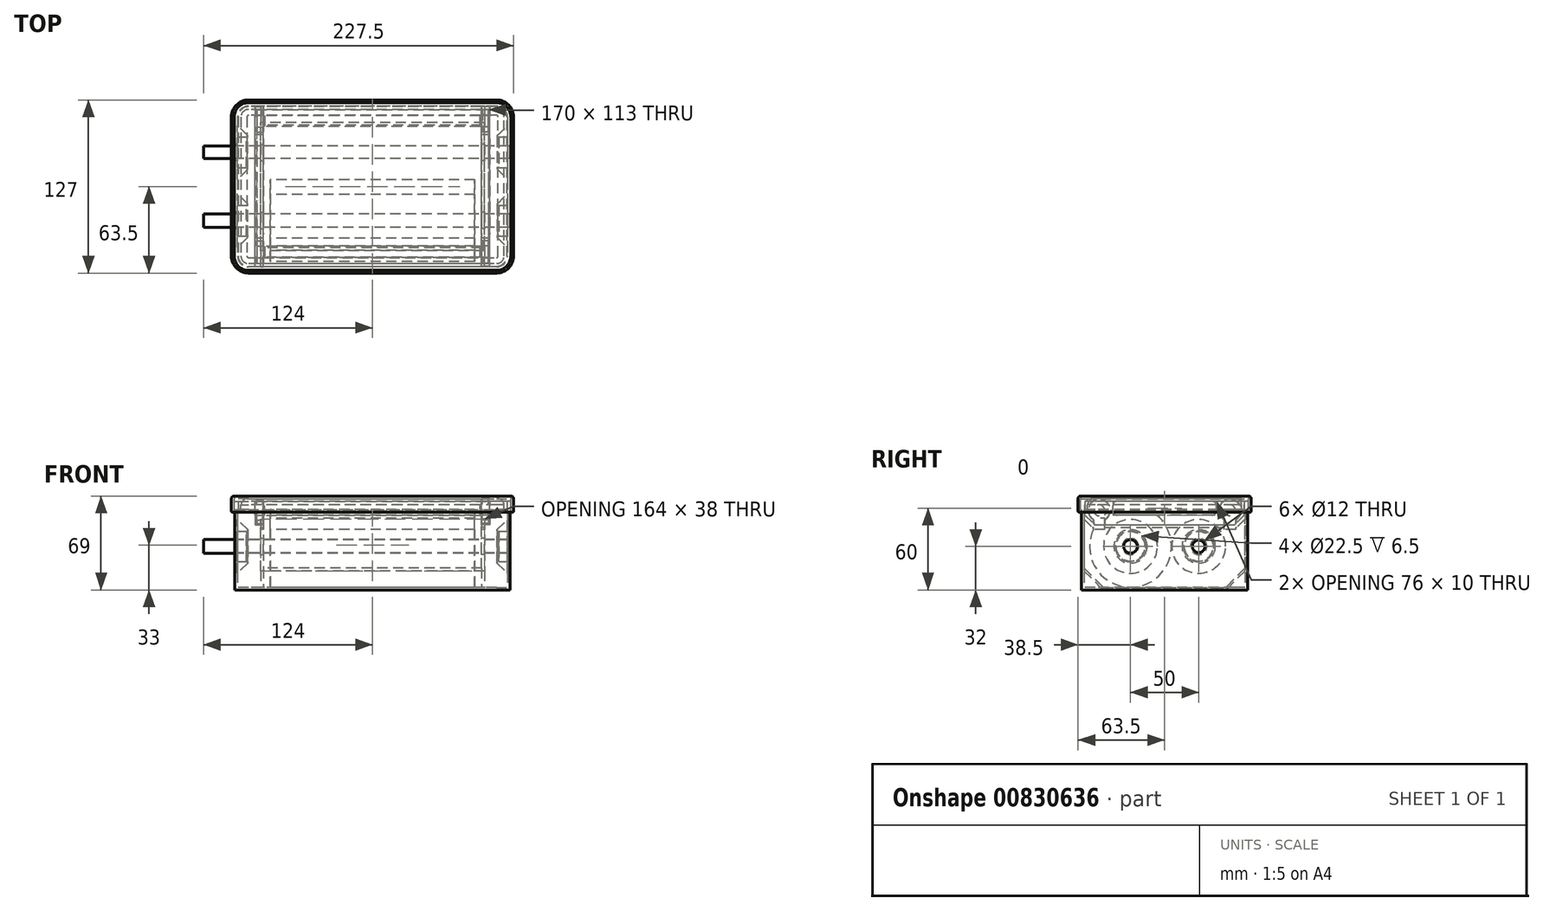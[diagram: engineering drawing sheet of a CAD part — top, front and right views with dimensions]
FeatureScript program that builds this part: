
annotation { "Feature Type Name" : "Feature", "Feature Type Description" : "" }
export const myFeature = defineFeature(function(context is Context, id is Id, definition is map)
    precondition{}
    {
        {
            var Q0;
            Q0=qCreatedBy(makeId("Top.planeOp"),FACE);
            var sketch = newSketch(context, id + "F0", { "sketchPlane" : qUnion([Q0])});
            skLineSegment(sketch, "E0.bottom", {"start": v(-100, 60) * mm, "end": v(100, 60) * mm});
            skLineSegment(sketch, "E0.top", {"start": v(-100, -60) * mm, "end": v(100, -60) * mm});
            skLineSegment(sketch, "E0.left", {"start": v(-100, 60) * mm, "end": v(-100, -60) * mm});
            skLineSegment(sketch, "E0.right", {"start": v(100, 60) * mm, "end": v(100, -60) * mm});
            skSolve(sketch);
        }
        {
            var Q0;
            Q0=qCreatedBy(makeId("Top.planeOp"),FACE);
            var sketch = newSketch(context, id + "F1", { "sketchPlane" : qUnion([Q0])});
            skLineSegment(sketch, "E1.bottom", {"start": v(-91, 61) * mm, "end": v(91, 61) * mm});
            skLineSegment(sketch, "E1.top", {"start": v(-91, -61) * mm, "end": v(91, -61) * mm});
            skLineSegment(sketch, "E1.left", {"start": v(-101, 51) * mm, "end": v(-101, -51) * mm});
            skLineSegment(sketch, "E1.right", {"start": v(101, 51) * mm, "end": v(101, -51) * mm});
            skPoint(sketch, "E2.visualSharp", {"position": v(-101, 61) * mm});
            skArc(sketch, "E2.filletArc", {"start": v(-91, 61) * mm, "mid": v(-98.07, 58.07) * mm, "end": v(-101, 51) * mm});
            skPoint(sketch, "E3.visualSharp", {"position": v(-101, -61) * mm});
            skArc(sketch, "E3.filletArc", {"start": v(-101, -51) * mm, "mid": v(-98.07, -58.07) * mm, "end": v(-91, -61) * mm});
            skPoint(sketch, "E4.visualSharp", {"position": v(101, -61) * mm});
            skArc(sketch, "E4.filletArc", {"start": v(91, -61) * mm, "mid": v(98.07, -58.07) * mm, "end": v(101, -51) * mm});
            skPoint(sketch, "E5.visualSharp", {"position": v(101, 61) * mm});
            skArc(sketch, "E5.filletArc", {"start": v(101, 51) * mm, "mid": v(98.07, 58.07) * mm, "end": v(91, 61) * mm});
            skSolve(sketch);
        }
        {
            var Q0;
            Q0=qCreatedBy(makeId("Top.planeOp"),FACE);
            var sketch = newSketch(context, id + "F2", { "sketchPlane" : qUnion([Q0])});
            skLineSegment(sketch, "E6.bottom", {"start": v(91, 59) * mm, "end": v(-91, 59) * mm});
            skLineSegment(sketch, "E6.top", {"start": v(91, -59) * mm, "end": v(-91, -59) * mm});
            skLineSegment(sketch, "E6.left", {"start": v(99, 51) * mm, "end": v(99, -51) * mm});
            skLineSegment(sketch, "E6.right", {"start": v(-99, 51) * mm, "end": v(-99, -51) * mm});
            skPoint(sketch, "E7.visualSharp", {"position": v(-99, -59) * mm});
            skArc(sketch, "E7.filletArc", {"start": v(-99, -51) * mm, "mid": v(-96.66, -56.66) * mm, "end": v(-91, -59) * mm});
            skPoint(sketch, "E8.visualSharp", {"position": v(-99, 59) * mm});
            skArc(sketch, "E8.filletArc", {"start": v(-91, 59) * mm, "mid": v(-96.66, 56.66) * mm, "end": v(-99, 51) * mm});
            skPoint(sketch, "E9.visualSharp", {"position": v(99, 59) * mm});
            skArc(sketch, "E9.filletArc", {"start": v(99, 51) * mm, "mid": v(96.66, 56.66) * mm, "end": v(91, 59) * mm});
            skPoint(sketch, "E10.visualSharp", {"position": v(99, -59) * mm});
            skArc(sketch, "E10.filletArc", {"start": v(91, -59) * mm, "mid": v(96.66, -56.66) * mm, "end": v(99, -51) * mm});
            skSolve(sketch);
        }
        {
            var Q0;
            Q0 = qSketchRegion(id + "F1", true);
            extrude(context, id + "F3", {"entities" : qUnion([Q0]), "flatOperationType" : FlatOperationType.REMOVE, "depth" : 57 * mm, "offsetDistance" : 25 * mm, "hasSecondDirection" : true, "secondDirectionOppositeDirection" : true, "secondDirectionDepth" : 2 * mm, "domain" : OperationDomain.MODEL});
        }
        {
            var Q0;
            Q0 = qSketchRegion(id + "F2", true);
            extrude(context, id + "F4", {"entities" : qUnion([Q0]), "depth" : 65 * mm, "offsetDistance" : 25 * mm});
        }
        {
            var Q0;
            Q0=makeQuery(id+"F4.opExtrude","SWEPT_BODY",BODY,{"disambiguationData":[OSD([sQuery(id+"F2.wireOp",EDGE,"E6.bottom"),sQuery(id+"F2.wireOp",EDGE,"E6.top"),sQuery(id+"F2.wireOp",EDGE,"E6.left"),sQuery(id+"F2.wireOp",EDGE,"E6.right"),sQuery(id+"F2.wireOp",EDGE,"E7.filletArc"),sQuery(id+"F2.wireOp",EDGE,"E8.filletArc"),sQuery(id+"F2.wireOp",EDGE,"E9.filletArc"),sQuery(id+"F2.wireOp",EDGE,"E10.filletArc")])]});
            var Q1;
            Q1=makeQuery(id+"F3.opExtrude","SWEPT_BODY",BODY,{"disambiguationData":[OSD([sQuery(id+"F1.wireOp",EDGE,"E1.bottom"),sQuery(id+"F1.wireOp",EDGE,"E1.top"),sQuery(id+"F1.wireOp",EDGE,"E1.left"),sQuery(id+"F1.wireOp",EDGE,"E1.right"),sQuery(id+"F1.wireOp",EDGE,"E2.filletArc"),sQuery(id+"F1.wireOp",EDGE,"E3.filletArc"),sQuery(id+"F1.wireOp",EDGE,"E4.filletArc"),sQuery(id+"F1.wireOp",EDGE,"E5.filletArc")])]});
            booleanBodies(context, id + "F5", {"operationType" : BooleanOperationType.SUBTRACTION, "tools" : qUnion([Q0]), "targets" : qUnion([Q1])});
        }
        {
            var Q0;
            Q0=sQuery(id+"F2.wireOp",EDGE,"E6.left");
            cPlane(context, id + "F6", {"entities" : qUnion([Q0]), "cplaneType" : CPlaneType.LINE_ANGLE, "offset" : 25 * mm, "angle" : 90 * degree, "width" : 150 * mm, "height" : 150 * mm});
        }
        {
            var Q0;
            Q0=sQuery(id+"F2.wireOp",EDGE,"E6.right");
            cPlane(context, id + "F7", {"entities" : qUnion([Q0]), "cplaneType" : CPlaneType.LINE_ANGLE, "offset" : 25 * mm, "angle" : 90 * degree, "width" : 150 * mm, "height" : 150 * mm});
        }
        {
            var Q0;
            Q0=qCreatedBy(id+"F6.planeOp",FACE);
            var sketch = newSketch(context, id + "F8", { "sketchPlane" : qUnion([Q0])});
            skCircle(sketch, "E11", {"center": v(-25, 30) * mm, "radius": 11.25 * mm});
            skCircle(sketch, "E12", {"center": v(25, 30) * mm, "radius": 11.25 * mm});
            skSolve(sketch);
        }
        {
            var Q0;
            Q0=qCreatedBy(id+"F7.planeOp",FACE);
            var sketch = newSketch(context, id + "F9", { "sketchPlane" : qUnion([Q0])});
            skCircle(sketch, "E13", {"center": v(25, 30) * mm, "radius": 11.25 * mm});
            skCircle(sketch, "E14", {"center": v(-25, 30) * mm, "radius": 11.25 * mm});
            skSolve(sketch);
        }
        {
            var Q0;
            Q0=sQuery(id+"F8.wireOp",VERTEX,"E12.center");
            var Q1;
            Q1=sQuery(id+"F8.wireOp",VERTEX,"E11.center");
            var Q2;
            Q2=sQuery(id+"F9.wireOp",VERTEX,"E14.center");
            cPlane(context, id + "F10", {"entities" : qUnion([Q0, Q1, Q2]), "cplaneType" : CPlaneType.THREE_POINT, "offset" : 25 * mm, "width" : 150 * mm, "height" : 150 * mm});
        }
        {
            var Q0;
            Q0=qCreatedBy(id+"F10.planeOp",FACE);
            var sketch = newSketch(context, id + "F11", { "sketchPlane" : qUnion([Q0])});
            skLineSegment(sketch, "E15", {"start": v(99, 36.25) * mm, "end": v(92.5, 36.25) * mm});
            skLineSegment(sketch, "E16", {"start": v(92.5, 36.25) * mm, "end": v(92.5, 35.75) * mm});
            skLineSegment(sketch, "E17", {"start": v(92.5, 35.75) * mm, "end": v(91.5, 36.25) * mm});
            skLineSegment(sketch, "E18", {"start": v(91.5, 36.25) * mm, "end": v(91.5, 37.25) * mm});
            skLineSegment(sketch, "E19", {"start": v(99, 44.75) * mm, "end": v(99, 36.25) * mm});
            skLineSegment(sketch, "E20", {"start": v(-99, 13.75) * mm, "end": v(-92.5, 13.75) * mm});
            skLineSegment(sketch, "E21", {"start": v(-92.5, 13.75) * mm, "end": v(-92.5, 14.25) * mm});
            skLineSegment(sketch, "E22", {"start": v(-92.5, 14.25) * mm, "end": v(-91.5, 13.75) * mm});
            skLineSegment(sketch, "E23", {"start": v(-91.5, 13.75) * mm, "end": v(-91.5, 12.75) * mm});
            skLineSegment(sketch, "E24", {"start": v(-99, 5.25) * mm, "end": v(-99, 13.75) * mm});
            skLineSegment(sketch, "E25", {"start": v(-99, -36.25) * mm, "end": v(-92.5, -36.25) * mm});
            skLineSegment(sketch, "E26", {"start": v(-92.5, -36.25) * mm, "end": v(-92.5, -35.75) * mm});
            skLineSegment(sketch, "E27", {"start": v(-92.5, -35.75) * mm, "end": v(-91.5, -36.25) * mm});
            skLineSegment(sketch, "E28", {"start": v(-91.5, -36.25) * mm, "end": v(-91.5, -37.25) * mm});
            skLineSegment(sketch, "E29", {"start": v(-99, -44.75) * mm, "end": v(-99, -36.25) * mm});
            skLineSegment(sketch, "E30", {"start": v(99, -13.75) * mm, "end": v(92.5, -13.75) * mm});
            skLineSegment(sketch, "E31", {"start": v(92.5, -13.75) * mm, "end": v(92.5, -14.25) * mm});
            skLineSegment(sketch, "E32", {"start": v(92.5, -14.25) * mm, "end": v(91.5, -13.75) * mm});
            skLineSegment(sketch, "E33", {"start": v(91.5, -13.75) * mm, "end": v(91.5, -12.75) * mm});
            skLineSegment(sketch, "E34", {"start": v(99, -5.25) * mm, "end": v(99, -13.75) * mm});
            skLineSegment(sketch, "E35", {"start": v(91.5, 37.25) * mm, "end": v(99, 44.75) * mm});
            skLineSegment(sketch, "E36", {"start": v(91.5, -12.75) * mm, "end": v(99, -5.25) * mm});
            skLineSegment(sketch, "E37", {"start": v(-91.5, -37.25) * mm, "end": v(-99, -44.75) * mm});
            skLineSegment(sketch, "E38", {"start": v(-91.5, 12.75) * mm, "end": v(-99, 5.25) * mm});
            skSolve(sketch);
        }
        {
            var Q0;
            Q0=makeQuery(id+"F11.imprint","IMPRINT",FACE,{"disambiguationData":[TD([[makeQuery(id+"F11.imprint","IMPRINT",EDGE,{"derivedFrom":sQuery(id+"F11.wireOp",EDGE,"E15")}),-1.0]])]});
            var Q1;
            Q1=sQuery(id+"F8.wireOp",EDGE,"E12");
            sweep(context, id + "F12", {"profiles" : qUnion([Q0]), "path" : qUnion([Q1])});
        }
        {
            var Q0;
            Q0=makeQuery(id+"F11.imprint","IMPRINT",FACE,{"disambiguationData":[TD([[makeQuery(id+"F11.imprint","IMPRINT",EDGE,{"derivedFrom":sQuery(id+"F11.wireOp",EDGE,"E30")}),-1.0]])]});
            var Q1;
            Q1=sQuery(id+"F8.wireOp",EDGE,"E11");
            sweep(context, id + "F13", {"profiles" : qUnion([Q0]), "path" : qUnion([Q1])});
        }
        {
            var Q0;
            Q0=makeQuery(id+"F11.imprint","IMPRINT",FACE,{"disambiguationData":[TD([[makeQuery(id+"F11.imprint","IMPRINT",EDGE,{"derivedFrom":sQuery(id+"F11.wireOp",EDGE,"E20")}),-1.0]])]});
            var Q1;
            Q1=sQuery(id+"F9.wireOp",EDGE,"E13");
            sweep(context, id + "F14", {"profiles" : qUnion([Q0]), "path" : qUnion([Q1])});
        }
        {
            var Q0;
            Q0=makeQuery(id+"F11.imprint","IMPRINT",FACE,{"disambiguationData":[TD([[makeQuery(id+"F11.imprint","IMPRINT",EDGE,{"derivedFrom":sQuery(id+"F11.wireOp",EDGE,"E25")}),-1.0]])]});
            var Q1;
            Q1=sQuery(id+"F9.wireOp",EDGE,"E14");
            sweep(context, id + "F15", {"profiles" : qUnion([Q0]), "path" : qUnion([Q1])});
        }
        {
            var Q0;
            Q0=qCreatedBy(id+"F7.planeOp",FACE);
            var sketch = newSketch(context, id + "F16", { "sketchPlane" : qUnion([Q0])});
            skCircle(sketch, "E39", {"center": v(-25, 30) * mm, "radius": 6 * mm});
            skCircle(sketch, "E40", {"center": v(25, 30) * mm, "radius": 6 * mm});
            skSolve(sketch);
        }
        {
            var Q0;
            Q0=makeQuery(id+"F16.imprint","IMPRINT",FACE,{"disambiguationData":[TD([[makeQuery(id+"F16.imprint","IMPRINT",EDGE,{"derivedFrom":sQuery(id+"F16.wireOp",EDGE,"E40")}),1.0]])]});
            var Q1;
            Q1=makeQuery(id+"F16.imprint","IMPRINT",FACE,{"disambiguationData":[TD([[makeQuery(id+"F16.imprint","IMPRINT",EDGE,{"derivedFrom":sQuery(id+"F16.wireOp",EDGE,"E39")}),1.0]])]});
            extrude(context, id + "F17", {"entities" : qUnion([Q0, Q1]), "depth" : 5 * mm, "offsetDistance" : 25 * mm, "symmetric" : true});
        }
        {
            var Q0;
            Q0=makeQuery(id+"F17.opExtrude","SWEPT_BODY",BODY,{"disambiguationData":[OSD([sQuery(id+"F16.wireOp",EDGE,"E40")])]});
            var Q1;
            Q1=makeQuery(id+"F17.opExtrude","SWEPT_BODY",BODY,{"disambiguationData":[OSD([sQuery(id+"F16.wireOp",EDGE,"E39")])]});
            var Q2;
            Q2=makeQuery(id+"F3.opExtrude","SWEPT_BODY",BODY,{"disambiguationData":[OSD([sQuery(id+"F1.wireOp",EDGE,"E1.bottom"),sQuery(id+"F1.wireOp",EDGE,"E1.top"),sQuery(id+"F1.wireOp",EDGE,"E1.left"),sQuery(id+"F1.wireOp",EDGE,"E1.right"),sQuery(id+"F1.wireOp",EDGE,"E2.filletArc"),sQuery(id+"F1.wireOp",EDGE,"E3.filletArc"),sQuery(id+"F1.wireOp",EDGE,"E4.filletArc"),sQuery(id+"F1.wireOp",EDGE,"E5.filletArc")])]});
            booleanBodies(context, id + "F18", {"operationType" : BooleanOperationType.SUBTRACTION, "tools" : qUnion([Q0, Q1]), "targets" : qUnion([Q2])});
        }
        {
            var Q0;
            Q0=qCreatedBy(id+"F7.planeOp",FACE);
            var sketch = newSketch(context, id + "F19", { "sketchPlane" : qUnion([Q0])});
            skCircle(sketch, "E41", {"center": v(25, 30) * mm, "radius": 4.65 * mm});
            skCircle(sketch, "E42", {"center": v(-25, 30) * mm, "radius": 5 * mm});
            skSolve(sketch);
        }
        {
            var Q0;
            Q0=makeQuery(id+"F19.imprint","IMPRINT",FACE,{"disambiguationData":[TD([[makeQuery(id+"F19.imprint","IMPRINT",EDGE,{"derivedFrom":sQuery(id+"F19.wireOp",EDGE,"E41")}),1.0]])]});
            var Q1;
            Q1=makeQuery(id+"F19.imprint","IMPRINT",FACE,{"disambiguationData":[TD([[makeQuery(id+"F19.imprint","IMPRINT",EDGE,{"derivedFrom":sQuery(id+"F19.wireOp",EDGE,"E42")}),1.0]])]});
            extrude(context, id + "F20", {"entities" : qUnion([Q0, Q1]), "depth" : 200 * mm, "offsetDistance" : 25 * mm, "hasSecondDirection" : true, "secondDirectionOppositeDirection" : true, "secondDirectionDepth" : 25 * mm});
        }
        {
            var Q0;
            Q0=qCreatedBy(makeId("Right.planeOp"),FACE);
            var sketch = newSketch(context, id + "F21", { "sketchPlane" : qUnion([Q0])});
            skCircle(sketch, "E43", {"center": v(25, 30) * mm, "radius": 30 * mm});
            skCircle(sketch, "E44", {"center": v(-25, 30) * mm, "radius": 30 * mm});
            skSolve(sketch);
        }
        {
            var Q0;
            {var subQ0=sQuery(id+"F21.wireOp",EDGE,"E44");var subQ1=sQuery(id+"F21.wireOp",EDGE,"E43");var subQ2=makeQuery(id+"F21.imprint","INTERSECT",VERTEX,{"disambiguationData":[OD(0.0)],"derivedFrom":[subQ1,subQ0]});Q0=makeQuery(id+"F21.imprint","IMPRINT",FACE,{"disambiguationData":[TD([[makeQuery(id+"F21.imprint","IMPRINT",EDGE,{"disambiguationData":[TD([[subQ2,1.0]])],"derivedFrom":subQ1}),-1.0]])]});}
            var Q1;
            {var subQ0=sQuery(id+"F21.wireOp",EDGE,"E44");var subQ1=sQuery(id+"F21.wireOp",EDGE,"E43");var subQ2=makeQuery(id+"F21.imprint","INTERSECT",VERTEX,{"disambiguationData":[OD(0.0)],"derivedFrom":[subQ1,subQ0]});Q1=makeQuery(id+"F21.imprint","IMPRINT",FACE,{"disambiguationData":[TD([[makeQuery(id+"F21.imprint","IMPRINT",EDGE,{"disambiguationData":[TD([[subQ2,1.0]])],"derivedFrom":subQ1}),1.0]])]});}
            extrude(context, id + "F22", {"entities" : qUnion([Q0, Q1]), "depth" : 150 * mm, "offsetDistance" : 25 * mm, "symmetric" : true});
        }
        {
            var Q0;
            Q0=qCreatedBy(makeId("Top.planeOp"),FACE);
            cPlane(context, id + "F23", {"entities" : qUnion([Q0]), "cplaneType" : CPlaneType.OFFSET, "offset" : 65 * mm, "width" : 150 * mm, "height" : 150 * mm});
        }
        {
            var Q0;
            Q0=qCreatedBy(makeId("Right.planeOp"),FACE);
            var sketch = newSketch(context, id + "F24", { "sketchPlane" : qUnion([Q0])});
            skLineSegment(sketch, "E45.bottom", {"start": v(-59, 65) * mm, "end": v(59, 65) * mm});
            skLineSegment(sketch, "E45.top", {"start": v(-59, 0) * mm, "end": v(59, 0) * mm});
            skLineSegment(sketch, "E45.left", {"start": v(-59, 65) * mm, "end": v(-59, 0) * mm});
            skLineSegment(sketch, "E45.right", {"start": v(59, 65) * mm, "end": v(59, 0) * mm});
            skSolve(sketch);
        }
        {
            var Q0;
            Q0=qCreatedBy(makeId("Right.planeOp"),FACE);
            var sketch = newSketch(context, id + "F25", { "sketchPlane" : qUnion([Q0])});
            skLineSegment(sketch, "E46", {"start": v(-59, 50) * mm, "end": v(-59, 12) * mm});
            skLineSegment(sketch, "E47", {"start": v(-47, 0) * mm, "end": v(47, 0) * mm});
            skLineSegment(sketch, "E48", {"start": v(59, 12) * mm, "end": v(59, 50) * mm});
            skLineSegment(sketch, "E49", {"start": v(-53, 44) * mm, "end": v(53, 44) * mm});
            skCircle(sketch, "E50", {"center": v(-25, 30) * mm, "radius": 6 * mm});
            skCircle(sketch, "E51", {"center": v(25, 30) * mm, "radius": 6 * mm});
            skPoint(sketch, "E52.visualSharp", {"position": v(59, 0) * mm});
            skLineSegment(sketch, "E53", {"start": v(59, 12) * mm, "end": v(47, 0) * mm});
            skPoint(sketch, "E54.visualSharp", {"position": v(-59, 0) * mm});
            skLineSegment(sketch, "E55", {"start": v(-59, 12) * mm, "end": v(-47, 0) * mm});
            skLineSegment(sketch, "E56", {"start": v(59, 50) * mm, "end": v(53, 44) * mm});
            skLineSegment(sketch, "E57", {"start": v(-59, 50) * mm, "end": v(-53, 44) * mm});
            skSolve(sketch);
        }
        {
            var Q0;
            Q0=makeQuery(id+"F25.imprint","IMPRINT",FACE,{"disambiguationData":[TD([[makeQuery(id+"F25.imprint","IMPRINT",EDGE,{"derivedFrom":sQuery(id+"F25.wireOp",EDGE,"E46")}),1.0]])]});
            extrude(context, id + "F26", {"entities" : qUnion([Q0]), "operationType" : NewBodyOperationType.ADD, "depth" : 82 * mm, "offsetDistance" : 25 * mm, "hasSecondDirection" : true, "secondDirectionOppositeDirection" : false, "secondDirectionDepth" : 80 * mm});
        }
        {
            var Q0;
            Q0=makeQuery(id+"F25.imprint","IMPRINT",FACE,{"disambiguationData":[TD([[makeQuery(id+"F25.imprint","IMPRINT",EDGE,{"derivedFrom":sQuery(id+"F25.wireOp",EDGE,"E46")}),1.0]])]});
            extrude(context, id + "F27", {"entities" : qUnion([Q0]), "operationType" : NewBodyOperationType.ADD, "oppositeDirection" : true, "depth" : 82 * mm, "offsetDistance" : 25 * mm, "hasSecondDirection" : true, "secondDirectionOppositeDirection" : true, "secondDirectionDepth" : 80 * mm});
        }
        {
            var Q0;
            Q0=qCreatedBy(makeId("Right.planeOp"),FACE);
            var sketch = newSketch(context, id + "F28", { "sketchPlane" : qUnion([Q0])});
            skLineSegment(sketch, "E58", {"start": v(59, 12) * mm, "end": v(59, 14) * mm});
            skLineSegment(sketch, "E59", {"start": v(59, 14) * mm, "end": v(45, 0) * mm});
            skLineSegment(sketch, "E60", {"start": v(45, 0) * mm, "end": v(47, 0) * mm});
            skLineSegment(sketch, "E61", {"start": v(47, 0) * mm, "end": v(59, 12) * mm});
            skLineSegment(sketch, "E62", {"start": v(-59, 14) * mm, "end": v(-45, 0) * mm});
            skLineSegment(sketch, "E63", {"start": v(-45, 0) * mm, "end": v(-47, 0) * mm});
            skLineSegment(sketch, "E64", {"start": v(-47, 0) * mm, "end": v(-59, 12) * mm});
            skLineSegment(sketch, "E65", {"start": v(-59, 12) * mm, "end": v(-59, 14) * mm});
            skSolve(sketch);
        }
        {
            var Q0;
            Q0 = qSketchRegion(id + "F28", true);
            extrude(context, id + "F29", {"entities" : qUnion([Q0]), "operationType" : NewBodyOperationType.ADD, "depth" : 160 * mm, "offsetDistance" : 25 * mm, "symmetric" : true});
        }
        {
            var Q0;
            Q0=qCreatedBy(makeId("Right.planeOp"),FACE);
            var sketch = newSketch(context, id + "F30", { "sketchPlane" : qUnion([Q0])});
            skCircle(sketch, "E66", {"center": v(-48, 56.5) * mm, "radius": 4 * mm});
            skCircle(sketch, "E67", {"center": v(48, 56.5) * mm, "radius": 4 * mm});
            skSolve(sketch);
        }
        {
            var Q0;
            Q0=qCreatedBy(makeId("Right.planeOp"),FACE);
            var sketch = newSketch(context, id + "F31", { "sketchPlane" : qUnion([Q0])});
            skCircle(sketch, "E68", {"center": v(-48, 56.5) * mm, "radius": 8.25 * mm});
            skCircle(sketch, "E69", {"center": v(48, 56.5) * mm, "radius": 8.25 * mm});
            skSolve(sketch);
        }
        {
            var Q0;
            Q0=qCreatedBy(makeId("Right.planeOp"),FACE);
            var sketch = newSketch(context, id + "F32", { "sketchPlane" : qUnion([Q0])});
            skCircle(sketch, "E70", {"center": v(48, 56.5) * mm, "radius": 7.9 * mm});
            skCircle(sketch, "E71", {"center": v(-48, 56.5) * mm, "radius": 7.9 * mm});
            skSolve(sketch);
        }
        {
            var Q0;
            Q0=makeQuery(id+"F30.imprint","IMPRINT",FACE,{"disambiguationData":[TD([[makeQuery(id+"F30.imprint","IMPRINT",EDGE,{"derivedFrom":sQuery(id+"F30.wireOp",EDGE,"E66")}),1.0]])]});
            var Q1;
            Q1=makeQuery(id+"F30.imprint","IMPRINT",FACE,{"disambiguationData":[TD([[makeQuery(id+"F30.imprint","IMPRINT",EDGE,{"derivedFrom":sQuery(id+"F30.wireOp",EDGE,"E67")}),1.0]])]});
            extrude(context, id + "F33", {"entities" : qUnion([Q0, Q1]), "depth" : 170 * mm, "offsetDistance" : 25 * mm, "symmetric" : true});
        }
        {
            var Q0;
            Q0=qCreatedBy(id+"F23.planeOp",FACE);
            var sketch = newSketch(context, id + "F34", { "sketchPlane" : qUnion([Q0])});
            skLineSegment(sketch, "E72.bottom", {"start": v(-91, 61.5) * mm, "end": v(91, 61.5) * mm});
            skLineSegment(sketch, "E72.top", {"start": v(-91, -61.5) * mm, "end": v(91, -61.5) * mm});
            skLineSegment(sketch, "E72.left", {"start": v(-101.5, 51) * mm, "end": v(-101.5, -51) * mm});
            skLineSegment(sketch, "E72.right", {"start": v(101.5, 51) * mm, "end": v(101.5, -51) * mm});
            skPoint(sketch, "E73.visualSharp", {"position": v(101.5, 61.5) * mm});
            skArc(sketch, "E73.filletArc", {"start": v(101.5, 51) * mm, "mid": v(98.42, 58.42) * mm, "end": v(91, 61.5) * mm});
            skPoint(sketch, "E74.visualSharp", {"position": v(101.5, -61.5) * mm});
            skArc(sketch, "E74.filletArc", {"start": v(91, -61.5) * mm, "mid": v(98.42, -58.42) * mm, "end": v(101.5, -51) * mm});
            skPoint(sketch, "E75.visualSharp", {"position": v(-101.5, -61.5) * mm});
            skArc(sketch, "E75.filletArc", {"start": v(-101.5, -51) * mm, "mid": v(-98.42, -58.42) * mm, "end": v(-91, -61.5) * mm});
            skPoint(sketch, "E76.visualSharp", {"position": v(-101.5, 61.5) * mm});
            skArc(sketch, "E76.filletArc", {"start": v(-91, 61.5) * mm, "mid": v(-98.42, 58.42) * mm, "end": v(-101.5, 51) * mm});
            skSolve(sketch);
        }
        {
            var Q0;
            Q0=qCreatedBy(makeId("Right.planeOp"),FACE);
            var sketch = newSketch(context, id + "F35", { "sketchPlane" : qUnion([Q0])});
            skLineSegment(sketch, "E77", {"start": v(-61.5, 65) * mm, "end": v(-61.5, 67) * mm});
            skLineSegment(sketch, "E78", {"start": v(-61.5, 67) * mm, "end": v(-61.5, 67) * mm});
            skLineSegment(sketch, "E79", {"start": v(-63.5, 65) * mm, "end": v(-63.5, 56) * mm});
            skLineSegment(sketch, "E80", {"start": v(-62.5, 55) * mm, "end": v(-62.5, 55) * mm});
            skLineSegment(sketch, "E81", {"start": v(-61.5, 56) * mm, "end": v(-61.5, 63) * mm});
            skLineSegment(sketch, "E82", {"start": v(-61.5, 63) * mm, "end": v(-58.5, 63) * mm});
            skLineSegment(sketch, "E83", {"start": v(-58.5, 63) * mm, "end": v(-58.5, 56) * mm});
            skLineSegment(sketch, "E84", {"start": v(-57.5, 55) * mm, "end": v(-57.49, 55) * mm});
            skLineSegment(sketch, "E85", {"start": v(-52.1, 65) * mm, "end": v(-61.5, 65) * mm});
            skPoint(sketch, "E86.visualSharp", {"position": v(-63.5, 67) * mm});
            skArc(sketch, "E86.filletArc", {"start": v(-61.5, 67) * mm, "mid": v(-62.91, 66.41) * mm, "end": v(-63.5, 65) * mm});
            skPoint(sketch, "E87.visualSharp", {"position": v(-63.5, 55) * mm});
            skArc(sketch, "E87.filletArc", {"start": v(-63.5, 56) * mm, "mid": v(-63.2, 55.3) * mm, "end": v(-62.5, 55) * mm});
            skPoint(sketch, "E88.visualSharp", {"position": v(-56.5, 55) * mm});
            skArc(sketch, "E88.filletArc", {"start": v(-57.49, 55) * mm, "mid": v(-56.83, 55.24) * mm, "end": v(-56.5, 55.86) * mm});
            skPoint(sketch, "E89.visualSharp", {"position": v(-58.5, 55) * mm});
            skArc(sketch, "E89.filletArc", {"start": v(-58.5, 56) * mm, "mid": v(-58.2, 55.3) * mm, "end": v(-57.5, 55) * mm});
            skPoint(sketch, "E90.visualSharp", {"position": v(-61.5, 55) * mm});
            skArc(sketch, "E90.filletArc", {"start": v(-62.5, 55) * mm, "mid": v(-61.8, 55.3) * mm, "end": v(-61.5, 56) * mm});
            skArc(sketch, "E91", {"start": v(-52.1, 65) * mm, "mid": v(-55.06, 63.56) * mm, "end": v(-56.5, 60.6) * mm});
            skLineSegment(sketch, "E92", {"start": v(-56.5, 55.86) * mm, "end": v(-56.5, 60.6) * mm});
            skSolve(sketch);
        }
        {
            var Q0;
            {var subQ0=sQuery(id+"F35.wireOp",EDGE,"E77");Q0=makeQuery(id+"F35.imprint","IMPRINT",FACE,{"disambiguationData":[TD([[makeQuery(id+"F35.imprint","IMPRINT",EDGE,{"derivedFrom":subQ0}),1.0]])]});}
            var Q1;
            {var subQ1=sQuery(id+"F35.wireOp",EDGE,"E83");Q1=makeQuery(id+"F35.imprint","IMPRINT",FACE,{"disambiguationData":[TD([[makeQuery(id+"F35.imprint","IMPRINT",EDGE,{"derivedFrom":subQ1}),1.0]])]});}
            var Q2;
            Q2=sQuery(id+"F34.wireOp",EDGE,"E72.top");
            var Q3;
            Q3=sQuery(id+"F34.wireOp",EDGE,"E74.filletArc");
            var Q4;
            Q4=sQuery(id+"F34.wireOp",EDGE,"E72.right");
            var Q5;
            Q5=sQuery(id+"F34.wireOp",EDGE,"E73.filletArc");
            var Q6;
            Q6=sQuery(id+"F34.wireOp",EDGE,"E72.bottom");
            var Q7;
            Q7=sQuery(id+"F34.wireOp",EDGE,"E76.filletArc");
            var Q8;
            Q8=sQuery(id+"F34.wireOp",EDGE,"E72.left");
            var Q9;
            Q9=sQuery(id+"F34.wireOp",EDGE,"E75.filletArc");
            sweep(context, id + "F36", {"profiles" : qUnion([Q0, Q1]), "path" : qUnion([Q2, Q3, Q4, Q5, Q6, Q7, Q8, Q9])});
        }
        {
            var Q0;
            Q0=makeQuery(id+"F34.imprint","IMPRINT",FACE,{"disambiguationData":[TD([[makeQuery(id+"F34.imprint","IMPRINT",EDGE,{"derivedFrom":sQuery(id+"F34.wireOp",EDGE,"E72.bottom")}),-1.0]])]});
            extrude(context, id + "F37", {"entities" : qUnion([Q0]), "depth" : 2 * mm, "offsetDistance" : 25 * mm});
        }
        {
            var Q0;
            Q0=makeQuery(id+"F34.imprint","IMPRINT",FACE,{"disambiguationData":[TD([[makeQuery(id+"F34.imprint","IMPRINT",EDGE,{"derivedFrom":sQuery(id+"F34.wireOp",EDGE,"E72.bottom")}),-1.0]])]});
            extrude(context, id + "F38", {"entities" : qUnion([Q0]), "oppositeDirection" : true, "depth" : 2 * mm, "offsetDistance" : 25 * mm});
        }
        {
            var Q0;
            Q0=qCreatedBy(id+"F23.planeOp",FACE);
            var sketch = newSketch(context, id + "F39", { "sketchPlane" : qUnion([Q0])});
            skLineSegment(sketch, "E93.bottom", {"start": v(-85, 56.5) * mm, "end": v(85, 56.5) * mm});
            skLineSegment(sketch, "E93.top", {"start": v(-85, -56.5) * mm, "end": v(85, -56.5) * mm});
            skLineSegment(sketch, "E93.left", {"start": v(-85, 56.5) * mm, "end": v(-85, -56.5) * mm});
            skLineSegment(sketch, "E93.right", {"start": v(85, 56.5) * mm, "end": v(85, -56.5) * mm});
            skSolve(sketch);
        }
        {
            var Q0;
            Q0=makeQuery(id+"F39.imprint","IMPRINT",FACE,{"disambiguationData":[TD([[makeQuery(id+"F39.imprint","IMPRINT",EDGE,{"derivedFrom":sQuery(id+"F39.wireOp",EDGE,"E93.bottom")}),-1.0]])]});
            extrude(context, id + "F40", {"entities" : qUnion([Q0]), "oppositeDirection" : true, "depth" : 5 * mm, "offsetDistance" : 25 * mm});
        }
        {
            var Q0;
            Q0=makeQuery(id+"F40.opExtrude","SWEPT_BODY",BODY,{"disambiguationData":[OSD([sQuery(id+"F39.wireOp",EDGE,"E93.bottom"),sQuery(id+"F39.wireOp",EDGE,"E93.top"),sQuery(id+"F39.wireOp",EDGE,"E93.left"),sQuery(id+"F39.wireOp",EDGE,"E93.right")])]});
            var Q1;
            Q1=makeQuery(id+"F38.opExtrude","SWEPT_BODY",BODY,{"disambiguationData":[OSD([sQuery(id+"F34.wireOp",EDGE,"E72.bottom"),sQuery(id+"F34.wireOp",EDGE,"E72.top"),sQuery(id+"F34.wireOp",EDGE,"E72.left"),sQuery(id+"F34.wireOp",EDGE,"E72.right"),sQuery(id+"F34.wireOp",EDGE,"E73.filletArc"),sQuery(id+"F34.wireOp",EDGE,"E74.filletArc"),sQuery(id+"F34.wireOp",EDGE,"E75.filletArc"),sQuery(id+"F34.wireOp",EDGE,"E76.filletArc")])]});
            booleanBodies(context, id + "F41", {"operationType" : BooleanOperationType.SUBTRACTION, "tools" : qUnion([Q0]), "targets" : qUnion([Q1])});
        }
        {
            var Q0;
            Q0=qCreatedBy(makeId("Right.planeOp"),FACE);
            var sketch = newSketch(context, id + "F42", { "sketchPlane" : qUnion([Q0])});
            skLineSegment(sketch, "E94.bottom", {"start": v(-51.5, 46) * mm, "end": v(51.5, 46) * mm});
            skLineSegment(sketch, "E94.top", {"start": v(-58.5, 65) * mm, "end": v(58.5, 65) * mm});
            skLineSegment(sketch, "E94.left", {"start": v(-58.5, 53) * mm, "end": v(-58.5, 65) * mm});
            skLineSegment(sketch, "E94.right", {"start": v(58.5, 53) * mm, "end": v(58.5, 65) * mm});
            skPoint(sketch, "E95.visualSharp", {"position": v(-58.5, 46) * mm});
            skPoint(sketch, "E96.visualSharp", {"position": v(58.5, 46) * mm});
            skLineSegment(sketch, "E97", {"start": v(58.5, 53) * mm, "end": v(51.5, 46) * mm});
            skLineSegment(sketch, "E98", {"start": v(-58.5, 53) * mm, "end": v(-51.5, 46) * mm});
            skSolve(sketch);
        }
        {
            var Q0;
            Q0=makeQuery(id+"F42.imprint","IMPRINT",FACE,{"disambiguationData":[TD([[makeQuery(id+"F42.imprint","IMPRINT",EDGE,{"derivedFrom":sQuery(id+"F42.wireOp",EDGE,"E94.bottom")}),1.0]])]});
            extrude(context, id + "F43", {"entities" : qUnion([Q0]), "depth" : 86 * mm, "offsetDistance" : 25 * mm, "hasSecondDirection" : true, "secondDirectionOppositeDirection" : false, "secondDirectionDepth" : 80 * mm});
        }
        {
            var Q0;
            Q0=makeQuery(id+"F42.imprint","IMPRINT",FACE,{"disambiguationData":[TD([[makeQuery(id+"F42.imprint","IMPRINT",EDGE,{"derivedFrom":sQuery(id+"F42.wireOp",EDGE,"E94.bottom")}),1.0]])]});
            extrude(context, id + "F44", {"entities" : qUnion([Q0]), "oppositeDirection" : true, "depth" : 86 * mm, "offsetDistance" : 25 * mm, "hasSecondDirection" : true, "secondDirectionOppositeDirection" : true, "secondDirectionDepth" : 80 * mm});
        }
        {
            var Q0;
            Q0 = qSketchRegion(id + "F31", true);
            extrude(context, id + "F45", {"entities" : qUnion([Q0]), "operationType" : NewBodyOperationType.REMOVE, "depth" : 85 * mm, "offsetDistance" : 25 * mm, "hasSecondDirection" : true, "secondDirectionOppositeDirection" : false, "secondDirectionDepth" : 80.5 * mm});
        }
        {
            var Q0;
            Q0 = qSketchRegion(id + "F32", true);
            extrude(context, id + "F46", {"entities" : qUnion([Q0]), "operationType" : NewBodyOperationType.REMOVE, "depth" : 81 * mm, "offsetDistance" : 25 * mm, "hasSecondDirection" : true, "secondDirectionOppositeDirection" : false, "secondDirectionDepth" : 79 * mm});
        }
        {
            var Q0;
            Q0 = qSketchRegion(id + "F31", true);
            extrude(context, id + "F47", {"entities" : qUnion([Q0]), "operationType" : NewBodyOperationType.REMOVE, "oppositeDirection" : true, "depth" : 85 * mm, "offsetDistance" : 25 * mm, "hasSecondDirection" : true, "secondDirectionOppositeDirection" : true, "secondDirectionDepth" : 80.5 * mm});
        }
        {
            var Q0;
            Q0 = qSketchRegion(id + "F32", true);
            extrude(context, id + "F48", {"entities" : qUnion([Q0]), "operationType" : NewBodyOperationType.REMOVE, "oppositeDirection" : true, "depth" : 81 * mm, "offsetDistance" : 25 * mm, "hasSecondDirection" : true, "secondDirectionOppositeDirection" : true, "secondDirectionDepth" : 79 * mm});
        }
        {
            var Q0;
            Q0=qCreatedBy(makeId("Right.planeOp"),FACE);
            var sketch = newSketch(context, id + "F49", { "sketchPlane" : qUnion([Q0])});
            skLineSegment(sketch, "E99.bottom", {"start": v(-35, 63) * mm, "end": v(35, 63) * mm});
            skLineSegment(sketch, "E99.top", {"start": v(-35, 53) * mm, "end": v(35, 53) * mm});
            skLineSegment(sketch, "E99.left", {"start": v(-38, 60) * mm, "end": v(-38, 56) * mm});
            skLineSegment(sketch, "E99.right", {"start": v(38, 60) * mm, "end": v(38, 56) * mm});
            skPoint(sketch, "E100.visualSharp", {"position": v(38, 63) * mm});
            skArc(sketch, "E100.filletArc", {"start": v(38, 60) * mm, "mid": v(37.12, 62.12) * mm, "end": v(35, 63) * mm});
            skPoint(sketch, "E101.visualSharp", {"position": v(38, 53) * mm});
            skArc(sketch, "E101.filletArc", {"start": v(35, 53) * mm, "mid": v(37.12, 53.88) * mm, "end": v(38, 56) * mm});
            skPoint(sketch, "E102.visualSharp", {"position": v(-38, 63) * mm});
            skArc(sketch, "E102.filletArc", {"start": v(-35, 63) * mm, "mid": v(-37.12, 62.12) * mm, "end": v(-38, 60) * mm});
            skPoint(sketch, "E103.visualSharp", {"position": v(-38, 53) * mm});
            skArc(sketch, "E103.filletArc", {"start": v(-38, 56) * mm, "mid": v(-37.12, 53.88) * mm, "end": v(-35, 53) * mm});
            skSolve(sketch);
        }
        {
            var Q0;
            Q0 = qSketchRegion(id + "F49", true);
            extrude(context, id + "F50", {"entities" : qUnion([Q0]), "operationType" : NewBodyOperationType.REMOVE, "depth" : 174 * mm, "offsetDistance" : 25 * mm, "symmetric" : true});
        }
        {
            var Q0;
            Q0=qCreatedBy(makeId("Right.planeOp"),FACE);
            var sketch = newSketch(context, id + "F51", { "sketchPlane" : qUnion([Q0])});
            skLineSegment(sketch, "E104.bottom", {"start": v(43.75, 50.5) * mm, "end": v(52.25, 50.5) * mm});
            skLineSegment(sketch, "E104.top", {"start": v(43.75, 42.5) * mm, "end": v(52.25, 42.5) * mm});
            skLineSegment(sketch, "E104.left", {"start": v(43.75, 50.5) * mm, "end": v(43.75, 42.5) * mm});
            skLineSegment(sketch, "E104.right", {"start": v(52.25, 50.5) * mm, "end": v(52.25, 42.5) * mm});
            skLineSegment(sketch, "E105.bottom", {"start": v(-52.25, 50.5) * mm, "end": v(-43.75, 50.5) * mm});
            skLineSegment(sketch, "E105.top", {"start": v(-52.25, 42.5) * mm, "end": v(-43.75, 42.5) * mm});
            skLineSegment(sketch, "E105.left", {"start": v(-52.25, 50.5) * mm, "end": v(-52.25, 42.5) * mm});
            skLineSegment(sketch, "E105.right", {"start": v(-43.75, 50.5) * mm, "end": v(-43.75, 42.5) * mm});
            skSolve(sketch);
        }
        {
            var Q0;
            Q0 = qSketchRegion(id + "F51", true);
            extrude(context, id + "F52", {"entities" : qUnion([Q0]), "operationType" : NewBodyOperationType.REMOVE, "depth" : 170 * mm, "offsetDistance" : 25 * mm, "symmetric" : true});
        }
    });
